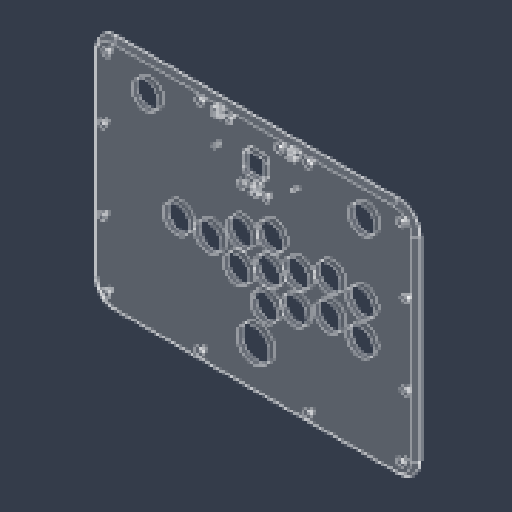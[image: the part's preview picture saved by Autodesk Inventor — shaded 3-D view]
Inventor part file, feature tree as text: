
AUTODESK INVENTOR PART (.ipt)
format: ipt  version: 2023.4 (Build 274418000, 418)  size: 303,104 bytes
history: native  units: mm
features: sketch x8, hole x5, extrude x3, mirror x2, fillet x1, chamfer x1
ambient origin geometry x8: Origin, YZ Plane, XZ Plane, XY Plane, X Axis, Y Axis, Z Axis, Center Point
bodies: Solid1 (feature_tree)
feature tree (20):
  extrude  "Extrusion1"  Depth=220.0mm
  hole  "Hole1"  [1 undecoded]
  hole  "Hole2"  [1 undecoded]
  hole  "Hole3"  [1 undecoded]
  fillet  "Fillet2"  Radius=65.3mm
  chamfer  "Chamfer1"  Distance=26.9mm
  hole  "Hole4"  [1 undecoded]
  mirror  "Mirror1"
  mirror  "Mirror2"
  extrude  "Extrusion5"  Depth=5.1mm
  hole  "Hole5"  [1 undecoded]
  extrude  "Extrusion6"  Depth=5.1mm
  sketch  "Sketch1"  dims[d0=300.0mm d1=220.0mm]
  sketch  "Sketch2"  dims[d3=0.0mm d4=40.0mm]
  sketch  "Sketch5"  dims[d5=15.5mm d6=26.3mm]
  sketch  "Sketch6"  dims[d7=29.5mm d11=52.4mm d12=65.3mm]
  sketch  "Sketch8"  dims[d13=65.2mm]
  sketch  "Sketch9"  dims[d14=9.7mm]
  sketch  "Sketch10"  dims[d15=29.4mm]
  sketch  "Sketch11"  dims[d16=2.6mm d17=26.9mm d18=29.6mm d19=29.5mm d20=1.7mm d22=46.0mm d23=30.1mm d24=96.7mm d25=91.7mm d26=31.0mm d27=31.0mm d28=35.0mm d29=25.0mm d30=6.0mm d31=3.6mm d32=2.0mm d33=90.0deg d34=8.0mm d35=20.594885mm d52=31.0mm d53=6.0mm d54=50.0mm d55=32.0mm d56=90.0deg d57=8.0mm d58=20.594885mm d61=30.0mm d62=50.0mm d63=1.482913mm d64=1.482913mm d65=40.0mm d66=40.0mm d67=71.4mm d68=38.8mm d69=3.4mm d70=6.0mm d71=4.4mm d72=2.3mm d73=90.0deg d74=8.0mm d75=20.594885mm d81=20.0mm d82=4.0mm d83=2.0mm d84=45.0deg d85=10.0mm d86=10.0mm d87=220.0mm d88=300.0mm d89=73.0mm d90=100.0mm d91=14.0mm d92=14.0mm d93=3.4mm d94=6.0mm d95=7.5mm d96=3.4mm d97=90.0deg d98=8.0mm d99=20.594885mm d100=20.0mm d101=20.0mm d102=2.0mm d103=4.0mm d104=0.0mm d105=0.0mm d106=22.5mm d107=18.0mm d108=22.5mm d109=22.5mm d110=27.4mm d111=68.8mm d112=3.4mm d113=6.0mm d114=7.5mm d115=2.9mm d116=90.0deg d117=8.0mm d118=20.594885mm d119=8.1mm d120=5.1mm d121=2.0mm d122=8.1mm d123=5.1mm d124=2.0mm d125=8.1mm d126=5.1mm d127=2.0mm d128=0.0mm d129=0.0mm d130=11.25mm d131=11.25mm d132=11.25mm]
note: 5 required parameter values undecoded (feature->parameter linkage not recoverable at this tier; creation-order binding heuristic only, values carry confidence <= 0.55)
